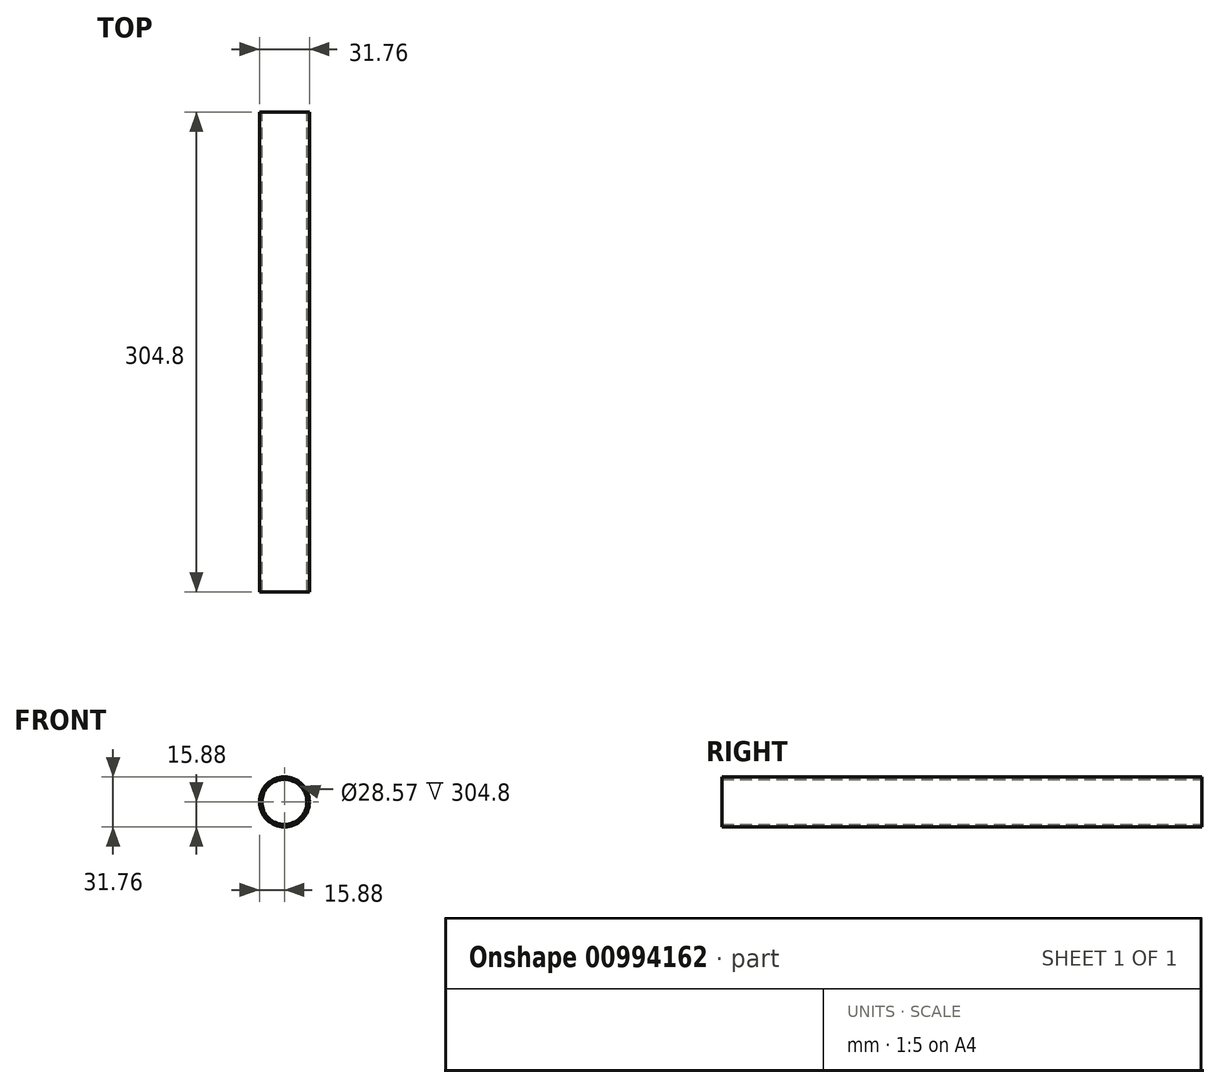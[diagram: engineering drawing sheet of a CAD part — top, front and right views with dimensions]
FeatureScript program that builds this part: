
annotation { "Feature Type Name" : "Feature", "Feature Type Description" : "" }
export const myFeature = defineFeature(function(context is Context, id is Id, definition is map)
    precondition{}
    {
        {
            var Q0;
            Q0=qCreatedBy(makeId("Front.planeOp"),FACE);
            var sketch = newSketch(context, id + "F0", { "sketchPlane" : qUnion([Q0])});
            skCircle(sketch, "E0", {"center": v(0, 0) * mm, "radius": 15.88 * mm});
            skCircle(sketch, "E1", {"center": v(0, 0) * mm, "radius": 14.29 * mm});
            skSolve(sketch);
        }
        {
            var Q0;
            Q0 = qSketchRegion(id + "F0", true);
            extrude(context, id + "F1", {"entities" : qUnion([Q0]), "depth" : 304.8 * mm, "offsetDistance" : 25.4 * mm});
        }
    });
